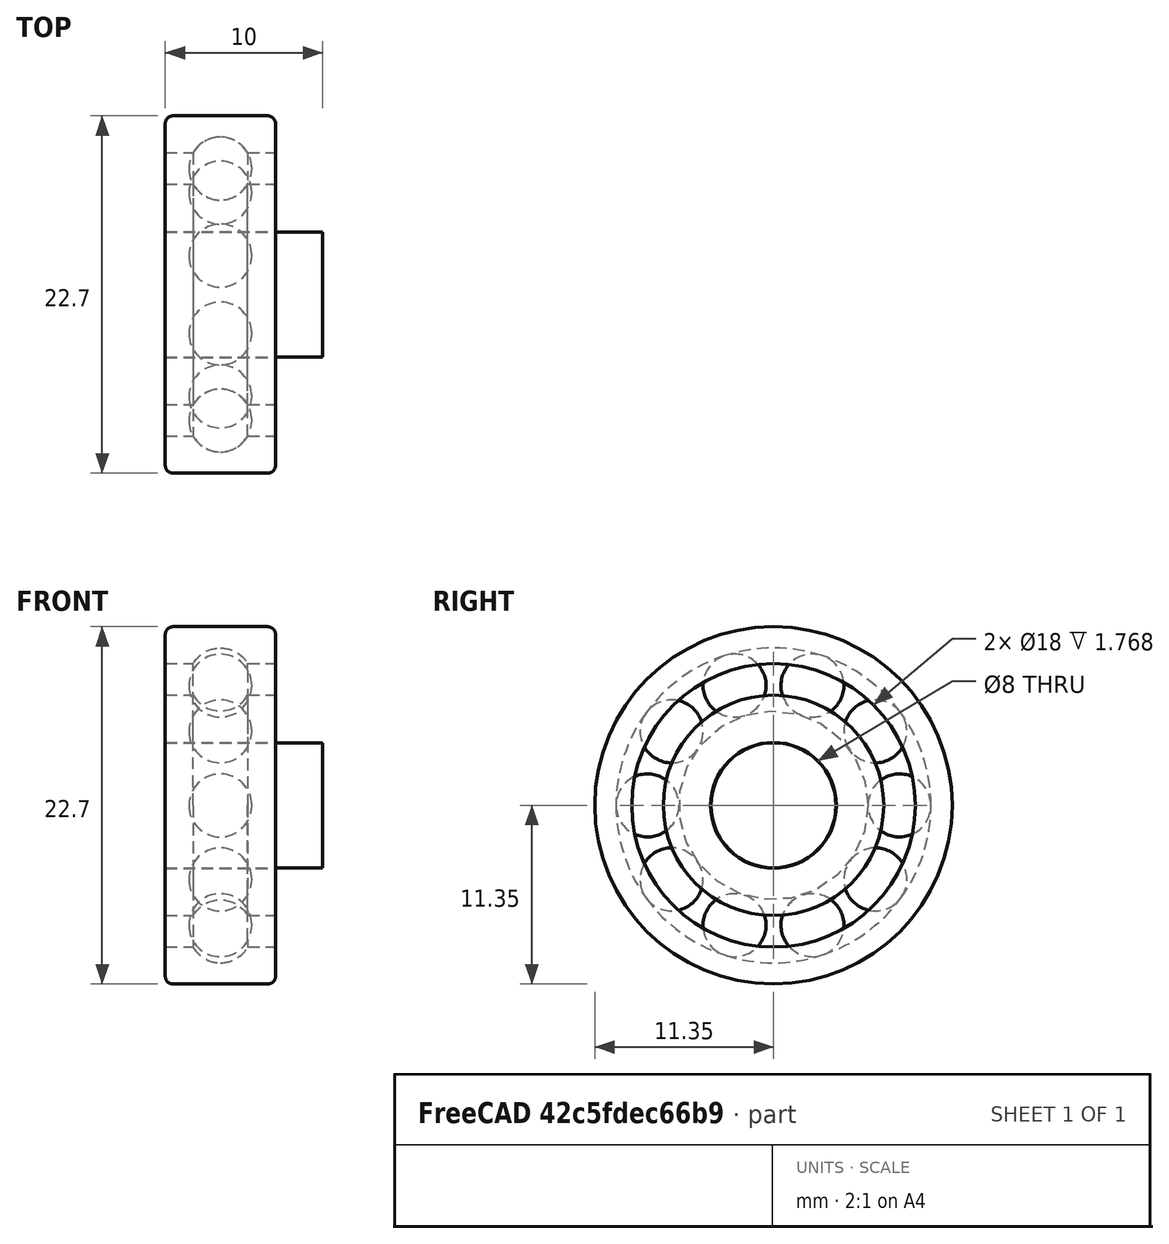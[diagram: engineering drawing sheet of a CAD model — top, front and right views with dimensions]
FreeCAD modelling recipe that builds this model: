
FCSTD DOCUMENT  (FreeCAD 0.18.4R)
Label: sp_balero(hoyo4mm)(ancho7mm)
License: All rights reserved
LicenseURL: http://en.wikipedia.org/wiki/All_rights_reserved
objects: Part::Cylinder×5, Part::Cut×3, Part::Torus×1, Part::Fuse×1, Part::Sphere×1, Part::FeaturePython×1, Part::Fillet×1, Part::MultiFuse×1
note: 14 computed .brp shape members not serialized (recipe doc carries the construction recipe); baked Part::Feature solids carry a one-line shape summary decoded from their .brp

FEATURE [Part::Cylinder] Cylinder  label="Cilindro"
  Angle = 360
  AttacherType = Attacher::AttachEngine3D
  Height = 7
  Radius = 11.35
FEATURE [Part::Cylinder] Cylinder001  label="Cilindro001"
  Angle = 360
  AttacherType = Attacher::AttachEngine3D
  Height = 10
  Radius = 9
FEATURE [Part::Cut] Cut  label="externo"
  Base = -> Cylinder
  Tool = -> Cylinder001
FEATURE [Part::Cylinder] Cylinder002  label="Cilindro002"
  Angle = 360
  AttacherType = Attacher::AttachEngine3D
  Height = 7
  Radius = 7
FEATURE [Part::Cylinder] Cylinder003  label="Cilindro003"
  Angle = 360
  AttacherType = Attacher::AttachEngine3D
  Height = 10
  Radius = 4
FEATURE [Part::Cut] Cut001  label="interno"
  Base = -> Cylinder002
  Tool = -> Cylinder003
FEATURE [Part::Torus] Torus  label="Toro"
  Angle1 = -180
  Angle2 = 180
  Angle3 = 360
  AttacherType = Attacher::AttachEngine3D
  Placement = pos=(0,0,3.5) rot=(0,0,1;0rad)
  Radius1 = 8
  Radius2 = 2
FEATURE [Part::Fuse] Fusion  label="balero aros"
  Base = -> Cut
  Tool = -> Cut001
FEATURE [Part::Cut] Cut002  label="struct"
  Base = -> Fusion
  Tool = -> Torus
FEATURE [Part::Sphere] Sphere  label="Esfera"
  Angle1 = -90
  Angle2 = 90
  Angle3 = 360
  AttacherType = Attacher::AttachEngine3D
  Placement = pos=(8,0,3.5) rot=(0,0,1;0rad)
  Radius = 2
FEATURE [Part::FeaturePython] Array  # Draft array (typed FeaturePython)
  Angle = 360
  ArrayType = 1
  Axis = (0,0,1)
  Base = -> Sphere
  Center = (0,0,0)
  Fuse = false
  IntervalAxis = (0,0,0)
  IntervalX = (1,0,0)
  IntervalY = (0,1,0)
  IntervalZ = (0,0,1)
  NumberPolar = 10
  NumberX = 2
  NumberY = 2
  NumberZ = 1
FEATURE [Part::Fillet] Fillet
  Base = -> Cut002
  Edges = 2 edges r=0.5: [Edge1,Edge3]
FEATURE [Part::MultiFuse] Fusion001  label="balero(hoyo4mm)"
  Placement = pos=(0,0,0) rot=(0.57735,0.57735,0.57735;2.0944rad)
  Shapes = -> [Array,Fillet]
FEATURE [Part::Cylinder] Cylinder004  label="auxiliar"
  Angle = 360
  AttacherType = Attacher::AttachEngine3D
  Height = 10
  Placement = pos=(0,0,0) rot=(0,1,0;1.5708rad)
  Radius = 3.97
